# Revit family: KingswayGroup_CntnsHngs_Anti-LigatureContinuousSwingHinge
name_source: partatom
category: Specialty Equipment
units: mm (PartAtom-declared; Revit-internal decimal feet)

## family parameters
Always vertical = No
Cut with Voids When Loaded = No
Part Type = Normal
Room Calculation Point = No
Round Connector Dimension = Use Diameter
Shared = No
Work Plane-Based = No

## types (1)
- KingswayGroup_CntnsHngs_Anti-LigatureContinuousSwingHinge
    AssetType = Fixed
    BIMObjectName = KingswayGroup_ContinuousHinges_Anti-LigatureContinuousSwingHinge
    Category = Pr_30_36_36_16:Continuous hinges
    Color = For full range of available finishes and colours, contact Kingsway Group
    Default Elevation = 0 mm  [stored 0 ft]
    Description = SwingHinge Continuous Hinge
    DurationUnit = year
    Features = The SwingHinge is a unique double action hinge that allows doors to swing 105° in both directions
    Finish = For full range of available finishes and colours, contact Kingsway Group
    HingeMaterial = NBS_Concept
    IfcExportAs = IfcDiscreteAccessoryType
    IfcExportType = USERDEFINED
    Length = 2200 mm
    Manufacturer = Kingsway Group
    ManufacturerName = Kingsway Group
    ManufacturerURL = https://kingswaygroupglobal.com
    Material = For full range of available material, contact Kingsway Group
    Model = KG202
    ModelNumber = KG202
    ModelReference = Anti-Ligature Continuous SwingHinge
    Name = ContinuousHinges_Anti-LigatureContinuousSwingHinge_KG202_KingswayGroup
    NominalHeight = 2200 mm
    NominalLength = 60 mm  [stored 0.19685 ft]
    NominalWidth = 45 mm  [stored 0.147638 ft]
    ProductInformation = https://kingswaygroupglobal.com
    Size = 60 x 2200 x 45 mm
    URL = https://kingswaygroupglobal.com
    Uniclass2015Code = Pr_30_36_36_16
    Uniclass2015Title = Continuous hinges
    Uniclass2015Version = Products v1.36
    Version = 1
    WarrantyDescription = 5-Year Guarantee *For faulty manufacture and not for damage
    WarrantyDurationParts = 5
    WarrantyDurationUnit = year

note: [stored X ft] marks values corroborated as IEEE doubles in the binary element streams (Revit-internal decimal feet)

## geometry (parser evidence)
native form markers: Sweep x2
no freeform markers — native parametric forms only
